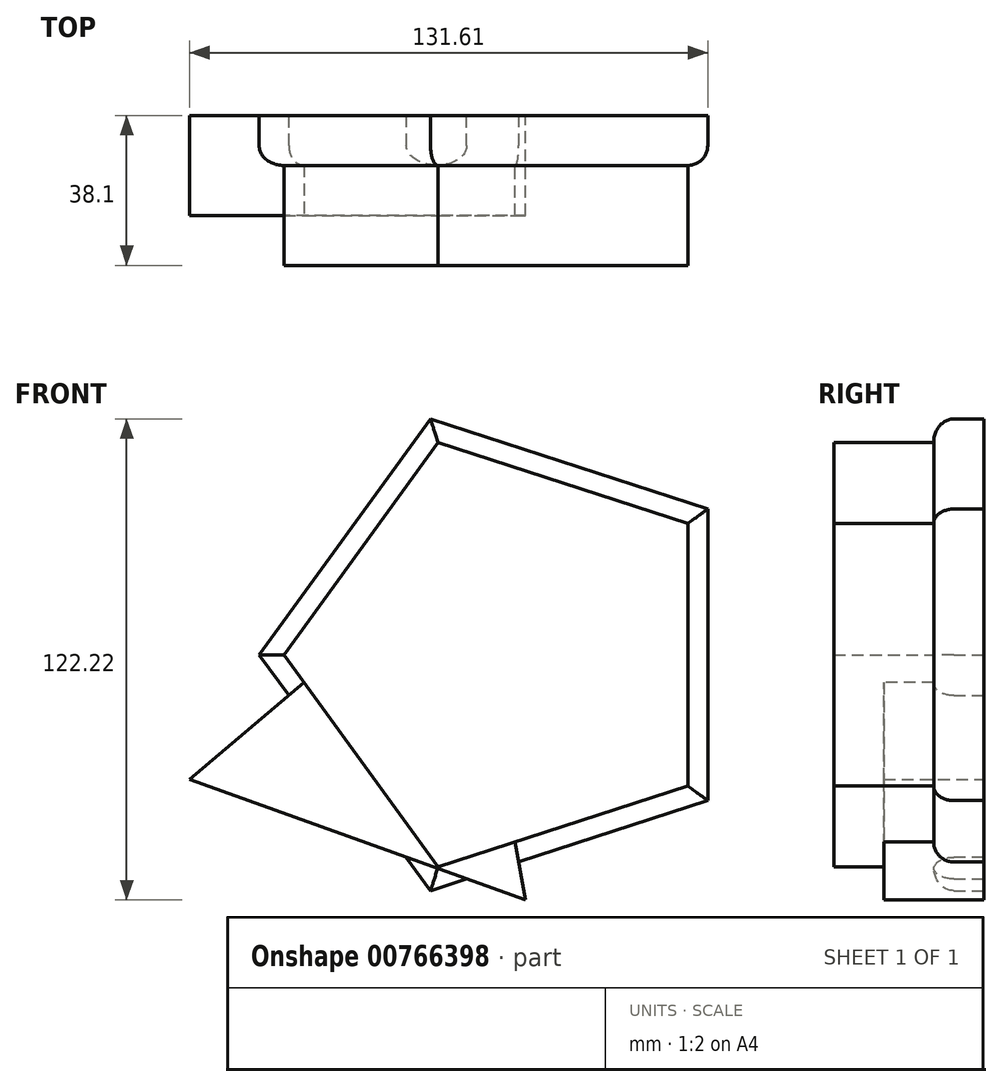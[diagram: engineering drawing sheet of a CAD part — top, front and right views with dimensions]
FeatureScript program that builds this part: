
annotation { "Feature Type Name" : "Feature", "Feature Type Description" : "" }
export const myFeature = defineFeature(function(context is Context, id is Id, definition is map)
    precondition{}
    {
        {
            var Q0;
            Q0=qCreatedBy(makeId("Front.planeOp"),FACE);
            var sketch = newSketch(context, id + "F0", { "sketchPlane" : qUnion([Q0])});
            skCircle(sketch, "E0.cCircle", {"center": v(0, 0) * mm, "radius": 50.97 * mm, "construction": true});
            skLineSegment(sketch, "E0.0", {"start": v(50.97, 37.03) * mm, "end": v(50.97, -37.03) * mm});
            skLineSegment(sketch, "E0.1", {"start": v(50.97, -37.03) * mm, "end": v(-19.47, -59.92) * mm});
            skLineSegment(sketch, "E0.2", {"start": v(-19.47, -59.92) * mm, "end": v(-63, 0) * mm});
            skLineSegment(sketch, "E0.3", {"start": v(-63, 0) * mm, "end": v(-19.47, 59.92) * mm});
            skLineSegment(sketch, "E0.4", {"start": v(-19.47, 59.92) * mm, "end": v(50.97, 37.03) * mm});
            skPoint(sketch, "E0.0.midPoint", {"position": v(50.97, 0) * mm});
            skSolve(sketch);
        }
        {
            var Q0;
            Q0=makeQuery(id+"F0.imprint","IMPRINT",FACE,{"disambiguationData":[TD([[makeQuery(id+"F0.imprint","IMPRINT",EDGE,{"derivedFrom":sQuery(id+"F0.wireOp",EDGE,"E0.0")}),-1.0]])]});
            extrude(context, id + "F1", {"entities" : qUnion([Q0]), "depth" : 12.7 * mm, "offsetDistance" : 25.4 * mm});
        }
        {
            var Q0;
            Q0=makeQuery(id+"F1.opExtrude","CAP_FACE",FACE,{"disambiguationData":[OSD([sQuery(id+"F0.wireOp",EDGE,"E0.0"),sQuery(id+"F0.wireOp",EDGE,"E0.1"),sQuery(id+"F0.wireOp",EDGE,"E0.2"),sQuery(id+"F0.wireOp",EDGE,"E0.3"),sQuery(id+"F0.wireOp",EDGE,"E0.4")])],"isStart":false});
            fillet(context, id + "F2", {"entities" : qUnion([Q0]), "radius" : 5.08 * mm, "tangentPropagation" : true, "allowEdgeOverflow" : false});
        }
        {
            var Q0;
            Q0=qCreatedBy(makeId("Front.planeOp"),FACE);
            var sketch = newSketch(context, id + "F3", { "sketchPlane" : qUnion([Q0])});
            skText(sketch, "E1", { "text": "D&M ", "fontName": "OpenSans-Bold.ttf"});
            const initialGuessF3  = {"E1": [-0.0422, -0.01214, 1, 0, 0.02527]};
            skSetInitialGuess(sketch, initialGuessF3);
            skSolve(sketch);
        }
        {
            var Q0;
            Q0=makeQuery(id+"F1.opExtrude","CAP_FACE",FACE,{"disambiguationData":[OSD([sQuery(id+"F0.wireOp",EDGE,"E0.0"),sQuery(id+"F0.wireOp",EDGE,"E0.1"),sQuery(id+"F0.wireOp",EDGE,"E0.2"),sQuery(id+"F0.wireOp",EDGE,"E0.3"),sQuery(id+"F0.wireOp",EDGE,"E0.4")])],"isStart":false});
            var Q1;
            Q1 = qSketchRegion(id + "F3", true);
            extrude(context, id + "F4", {"entities" : qUnion([Q0, Q1]), "operationType" : NewBodyOperationType.ADD, "depth" : 25.4 * mm, "offsetDistance" : 25.4 * mm});
        }
        {
            var Q0;
            Q0=qCreatedBy(makeId("Front.planeOp"),FACE);
            var sketch = newSketch(context, id + "F5", { "sketchPlane" : qUnion([Q0])});
            skCircle(sketch, "E2.cCircle", {"center": v(-29.13, -22.37) * mm, "radius": 26.17 * mm, "construction": true});
            skLineSegment(sketch, "E2.0", {"start": v(-11.46, 26.9) * mm, "end": v(4.7, -62.3) * mm});
            skLineSegment(sketch, "E2.1", {"start": v(4.7, -62.3) * mm, "end": v(-80.64, -31.7) * mm});
            skLineSegment(sketch, "E2.2", {"start": v(-80.64, -31.7) * mm, "end": v(-11.46, 26.9) * mm});
            skPoint(sketch, "E2.0.midPoint", {"position": v(-3.38, -17.7) * mm});
            skSolve(sketch);
        }
        {
            var Q0;
            Q0=makeQuery(id+"F5.imprint","IMPRINT",FACE,{"disambiguationData":[TD([[makeQuery(id+"F5.imprint","IMPRINT",EDGE,{"derivedFrom":sQuery(id+"F5.wireOp",EDGE,"E2.0")}),-1.0]])]});
            extrude(context, id + "F6", {"entities" : qUnion([Q0]), "operationType" : NewBodyOperationType.ADD, "depth" : 25.4 * mm, "offsetDistance" : 25.4 * mm});
        }
    });
